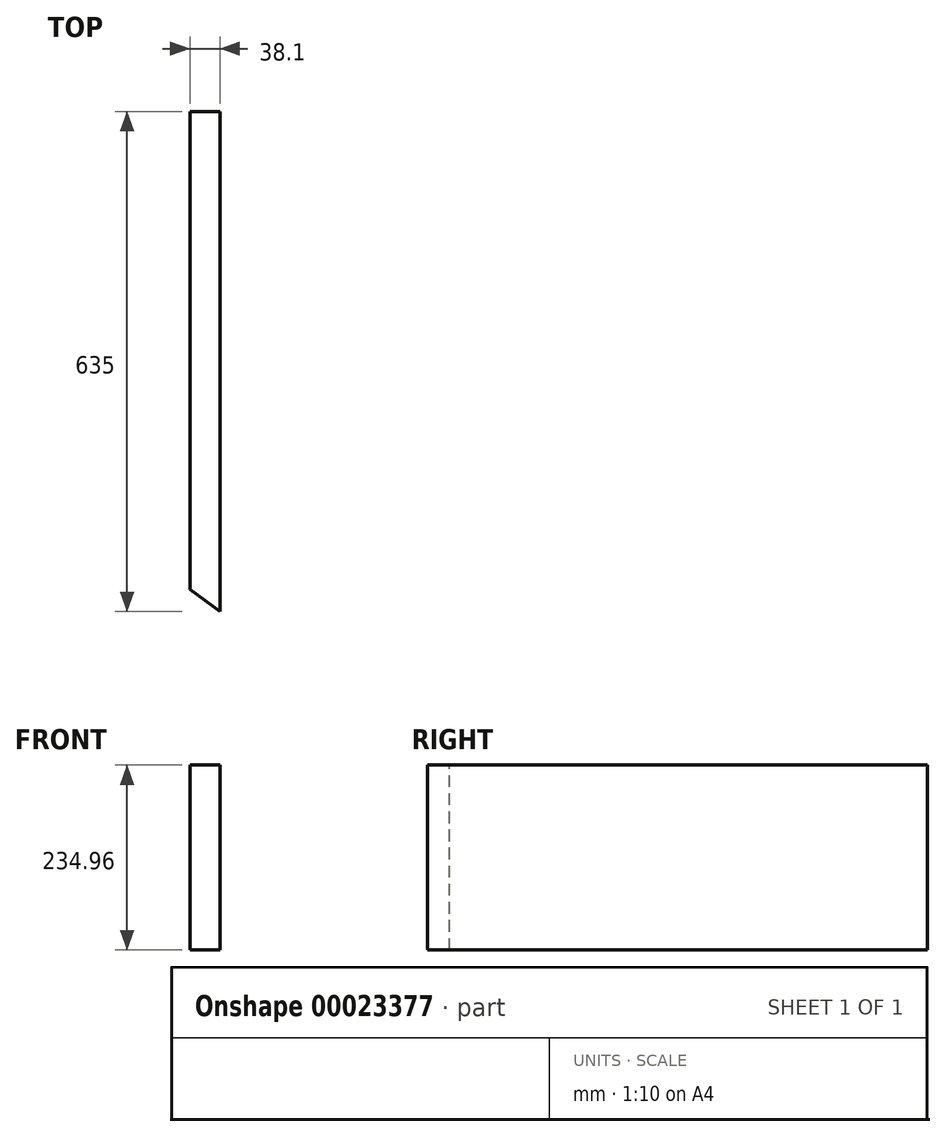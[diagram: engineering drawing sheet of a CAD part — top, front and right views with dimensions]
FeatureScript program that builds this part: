
annotation { "Feature Type Name" : "Feature", "Feature Type Description" : "" }
export const myFeature = defineFeature(function(context is Context, id is Id, definition is map)
    precondition{}
    {
        {
            var Q0;
            Q0=qCreatedBy(makeId("Front.planeOp"),FACE);
            var sketch = newSketch(context, id + "F0", { "sketchPlane" : qUnion([Q0])});
            skLineSegment(sketch, "E0.rect.bottom", {"start": v(-19.05, -117.47) * mm, "end": v(19.05, -117.47) * mm});
            skLineSegment(sketch, "E0.rect.top", {"start": v(-19.05, 117.48) * mm, "end": v(19.05, 117.48) * mm});
            skLineSegment(sketch, "E0.rect.left", {"start": v(-19.05, -117.47) * mm, "end": v(-19.05, 117.48) * mm});
            skLineSegment(sketch, "E0.rect.right", {"start": v(19.05, -117.47) * mm, "end": v(19.05, 117.48) * mm});
            skPoint(sketch, "E0.rect.middle", {"position": v(0, 0) * mm});
            skSolve(sketch);
        }
        {
            var Q0;
            Q0=makeQuery(id+"F0.imprint","IMPRINT",FACE,{"disambiguationData":[TD([[makeQuery(id+"F0.imprint","IMPRINT",EDGE,{"derivedFrom":sQuery(id+"F0.wireOp",EDGE,"E0.rect.bottom")}),1.0]])]});
            extrude(context, id + "F1", {"entities" : qUnion([Q0]), "endBound" : BoundingType.SYMMETRIC, "depth" : 635 * mm});
        }
        {
            var Q0;
            Q0=makeQuery(id+"F1.opExtrude","SWEPT_FACE",FACE,{"disambiguationData":[OSD([sQuery(id+"F0.wireOp",EDGE,"E0.rect.top")])]});
            var sketch = newSketch(context, id + "F2", { "sketchPlane" : qUnion([Q0])});
            skLineSegment(sketch, "E1", {"start": v(19.05, -317.5) * mm, "end": v(-19.05, -289.7) * mm});
            skLineSegment(sketch, "E2", {"start": v(-19.05, -289.7) * mm, "end": v(-19.05, -317.5) * mm});
            skLineSegment(sketch, "E3", {"start": v(-19.05, -317.5) * mm, "end": v(19.05, -317.5) * mm});
            skSolve(sketch);
        }
        {
            var Q0;
            Q0 = qSketchRegion(id + "F2", true);
            extrude(context, id + "F3", {"entities" : qUnion([Q0]), "operationType" : NewBodyOperationType.REMOVE, "endBound" : BoundingType.THROUGH_ALL, "oppositeDirection" : true, "depth" : 25.4 * mm});
        }
    });
